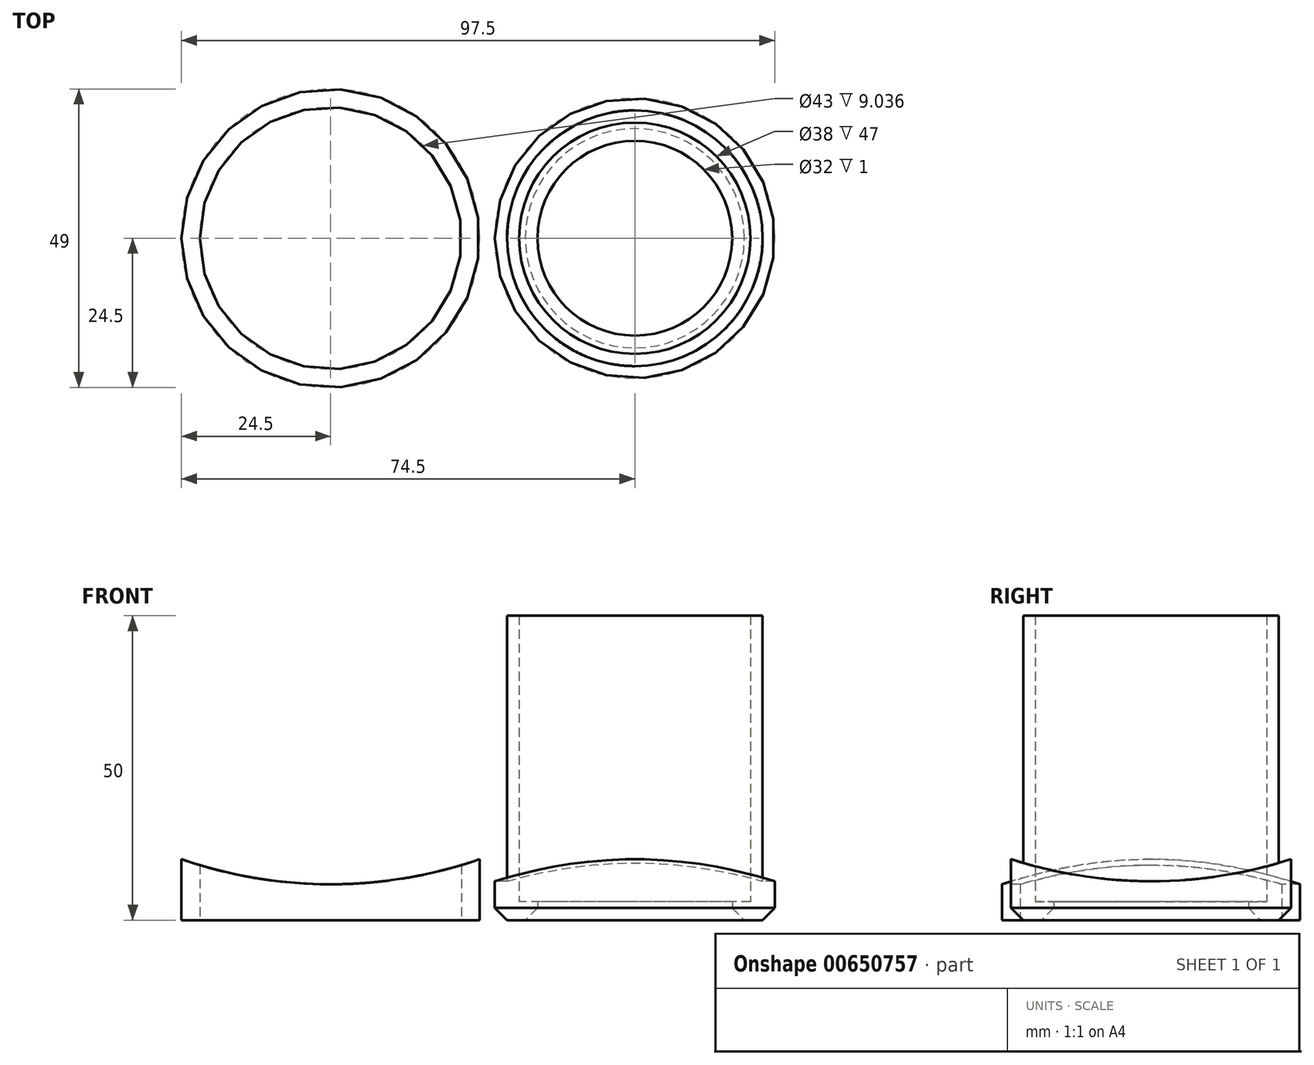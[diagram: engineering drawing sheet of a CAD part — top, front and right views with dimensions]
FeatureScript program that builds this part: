
annotation { "Feature Type Name" : "Feature", "Feature Type Description" : "" }
export const myFeature = defineFeature(function(context is Context, id is Id, definition is map)
    precondition{}
    {
        {
            var Q0;
            Q0=qCreatedBy(makeId("Top.planeOp"),FACE);
            var sketch = newSketch(context, id + "F0", { "sketchPlane" : qUnion([Q0])});
            skCircle(sketch, "E0", {"center": v(0, 0) * mm, "radius": 23 * mm});
            skCircle(sketch, "E1", {"center": v(0, 0) * mm, "radius": 16 * mm});
            skSolve(sketch);
        }
        {
            var Q0;
            Q0=makeQuery(id+"F0.imprint","IMPRINT",FACE,{"disambiguationData":[TD([[makeQuery(id+"F0.imprint","IMPRINT",EDGE,{"derivedFrom":sQuery(id+"F0.wireOp",EDGE,"E0")}),1.0]])]});
            extrude(context, id + "F1", {"entities" : qUnion([Q0]), "depth" : 3 * mm, "offsetDistance" : 25 * mm});
        }
        {
            var Q0;
            Q0=makeQuery(id+"F1.opExtrude","CAP_FACE",FACE,{"disambiguationData":[OSD([sQuery(id+"F0.wireOp",EDGE,"E0"),sQuery(id+"F0.wireOp",EDGE,"E1")])],"isStart":false});
            var sketch = newSketch(context, id + "F2", { "sketchPlane" : qUnion([Q0])});
            skCircle(sketch, "E2", {"center": v(0, 0) * mm, "radius": 19 * mm});
            skSolve(sketch);
        }
        {
            var Q0;
            Q0=makeQuery(id+"F2.imprint","IMPRINT",FACE,{"disambiguationData":[TD([[makeQuery(id+"F2.imprint","IMPRINT",EDGE,{"derivedFrom":sQuery(id+"F2.wireOp",EDGE,"E2")}),-1.0]])]});
            extrude(context, id + "F3", {"entities" : qUnion([Q0]), "operationType" : NewBodyOperationType.ADD, "depth" : 25 * mm, "offsetDistance" : 25 * mm});
        }
        {
            var Q0;
            Q0=qCreatedBy(makeId("Right.planeOp"),FACE);
            var sketch = newSketch(context, id + "F4", { "sketchPlane" : qUnion([Q0])});
            skArc(sketch, "E3", {"start": v(-23, 10) * mm, "mid": v(0, 6.39) * mm, "end": v(23, 10) * mm});
            skPoint(sketch, "E4", {"position": v(-23, 0) * mm});
            skPoint(sketch, "E5", {"position": v(23, 0) * mm});
            skLineSegment(sketch, "E6", {"start": v(-23, 10) * mm, "end": v(-32.47, 33.88) * mm});
            skLineSegment(sketch, "E7", {"start": v(-32.47, 33.88) * mm, "end": v(36.38, 33.88) * mm});
            skLineSegment(sketch, "E8", {"start": v(36.38, 33.88) * mm, "end": v(23, 10) * mm});
            skSolve(sketch);
        }
        {
            var Q0;
            Q0=makeQuery(id+"F4.imprint","IMPRINT",FACE,{"disambiguationData":[TD([[makeQuery(id+"F4.imprint","IMPRINT",EDGE,{"derivedFrom":sQuery(id+"F4.wireOp",EDGE,"E3")}),1.0]])]});
            extrude(context, id + "F5", {"entities" : qUnion([Q0]), "operationType" : NewBodyOperationType.REMOVE, "endBound" : BoundingType.SYMMETRIC, "depth" : 100 * mm, "offsetDistance" : 25 * mm});
        }
        {
            var Q0;
            Q0=qCreatedBy(makeId("Top.planeOp"),FACE);
            var sketch = newSketch(context, id + "F6", { "sketchPlane" : qUnion([Q0])});
            skCircle(sketch, "E9", {"center": v(0, 0) * mm, "radius": 19 * mm});
            skCircle(sketch, "E10", {"center": v(0, 0) * mm, "radius": 21 * mm});
            skSolve(sketch);
        }
        {
            var Q0;
            Q0=makeQuery(id+"F6.imprint","IMPRINT",FACE,{"disambiguationData":[TD([[makeQuery(id+"F6.imprint","IMPRINT",EDGE,{"derivedFrom":sQuery(id+"F6.wireOp",EDGE,"E9")}),-1.0]])]});
            extrude(context, id + "F7", {"entities" : qUnion([Q0]), "operationType" : NewBodyOperationType.ADD, "depth" : 50 * mm, "offsetDistance" : 25 * mm});
        }
        {
            var Q0;
            Q0=qCreatedBy(makeId("Top.planeOp"),FACE);
            var sketch = newSketch(context, id + "F8", { "sketchPlane" : qUnion([Q0])});
            skCircle(sketch, "E11", {"center": v(-50, 0) * mm, "radius": 24.5 * mm});
            skCircle(sketch, "E12", {"center": v(-50, 0) * mm, "radius": 21.5 * mm});
            skSolve(sketch);
        }
        {
            var Q0;
            Q0=makeQuery(id+"F8.imprint","IMPRINT",FACE,{"disambiguationData":[TD([[makeQuery(id+"F8.imprint","IMPRINT",EDGE,{"derivedFrom":sQuery(id+"F8.wireOp",EDGE,"E11")}),1.0]])]});
            extrude(context, id + "F9", {"entities" : qUnion([Q0]), "depth" : 25 * mm, "offsetDistance" : 25 * mm});
        }
        {
            var Q0;
            Q0=qCreatedBy(makeId("Front.planeOp"),FACE);
            var sketch = newSketch(context, id + "F10", { "sketchPlane" : qUnion([Q0])});
            skArc(sketch, "E13", {"start": v(-74.5, 10) * mm, "mid": v(-50, 5.89) * mm, "end": v(-25.5, 10) * mm});
            skPoint(sketch, "E14", {"position": v(-74.5, 0) * mm});
            skPoint(sketch, "E15", {"position": v(-25.5, 0) * mm});
            skLineSegment(sketch, "E16", {"start": v(-74.5, 10) * mm, "end": v(-81.32, 36.65) * mm});
            skLineSegment(sketch, "E17", {"start": v(-81.32, 36.65) * mm, "end": v(-22.98, 35.57) * mm});
            skLineSegment(sketch, "E18", {"start": v(-22.98, 35.57) * mm, "end": v(-25.5, 10) * mm});
            skSolve(sketch);
        }
        {
            var Q0;
            Q0=makeQuery(id+"F10.imprint","IMPRINT",FACE,{"disambiguationData":[TD([[makeQuery(id+"F10.imprint","IMPRINT",EDGE,{"derivedFrom":sQuery(id+"F10.wireOp",EDGE,"E13")}),1.0]])]});
            extrude(context, id + "F11", {"entities" : qUnion([Q0]), "operationType" : NewBodyOperationType.REMOVE, "endBound" : BoundingType.SYMMETRIC, "oppositeDirection" : true, "depth" : 100 * mm, "offsetDistance" : 25 * mm});
        }
        {
            var Q0;
            Q0=makeQuery(id+"F1.opExtrude","CAP_EDGE",EDGE,{"disambiguationData":[OSD([sQuery(id+"F0.wireOp",EDGE,"E0")])],"isStart":true});
            var Q1;
            Q1=makeQuery(id+"F1.opExtrude","CAP_EDGE",EDGE,{"disambiguationData":[OSD([sQuery(id+"F0.wireOp",EDGE,"E1")])],"isStart":true});
            chamfer(context, id + "F12", {"entities" : qUnion([Q0, Q1]), "width" : 2 * mm, "tangentPropagation" : true});
        }
    });
